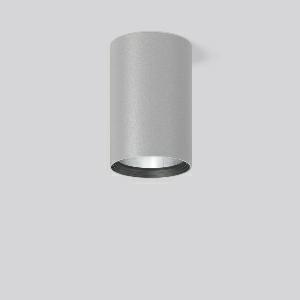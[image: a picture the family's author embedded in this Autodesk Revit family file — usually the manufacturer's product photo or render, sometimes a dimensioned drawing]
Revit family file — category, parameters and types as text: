
# Revit family: heledon_maxi_a_931224_004_76_19c8
name_source: partatom
category: Lighting Fixtures
units: mm (PartAtom-declared; Revit-internal decimal feet)

## family parameters
Cut with Voids When Loaded = No
Host = Face
Light Source = No
Part Type = Normal
Room Calculation Point = No
Round Connector Dimension = Use Diameter
Shared = No

## types (1)
- HELEDON maxi A (1 x LED Modul 930, 4300 lm, 3000)
    Apparent Load = 35 VA
    Approval mark = CE
    CIE Flux Codes = 100 100 100 100 100
    Color Rendering = 90
    Color Temperature = 3000
    Default Elevation = 1800 mm
    Description = Series: HELEDON maxi
Cylindrical surface-mounted downlight. Housing: die-cast aluminium, powder-coated. Internal ceiling frame polycarbonate with bayonet mounting. Black plastic ring and recessed LED to prevent glare from the side. Optical assembly with reflector made of MIRO-Silver with 98% total light reflection for outstanding efficiency - can be changed without tools. Best colour rendering index Ra>90. Suitable for Ceiling mounting. Easy installation with a separate ceiling frame with bayonet mounting and plug connection. Driver integrated. Connected via plug-in connector. High quality converter without flickering and stroboscopic effect. The following accessories can be mounted without use of tools: interchangeable lenses, decorative glasses, honeycomb louvre, clear and frosted diffusers, white interchangeable plastic ring. 
Colour: silver
Diameter: 123 mm
Height: 183 mm
Lamp: LED
Socket: without socket
Colour temperature: 3000K
Colour rendering index (CRI): 92
System power: 35 W
Rated luminous flux: 4300 lm
Luminous efficiency: 123 lm/W
Control gear: Converter, dimmable, DALI
Protection class: I
Type of protection: IP 20
    Height = 183 mm
    Lamp = 1 x LED Modul 930
    Lamp Light Flux = 4300 lm
    Lamp count = 1
    Length = 123 mm
    Lifetime = 50000 h
    Luminous efficacy = 123 lm/W
    Manufacturer = RZB
    ModVariant = No
    Model = 931224.004.76
    Mounting Place = Ceiling
    Mounting Type = Surface mounted
    Number of Poles = 1
    OnlyDefault = Yes
    Power Factor = 1
    Product Name = HELEDON maxi A
    Product group = Surface mounted downlights
    ProductGroupID = 302
    Protection Class = Protection class I
    Protection Degree = IP 20
    RLX_Detail_Level = 1
    RLX_Emergency_Light_Flux = 0 lm
    RLX_Emergency_Type = 0
    RLX_Emergency_Type_DB = No
    RlxData = <blob elided: 100297 chars, md5=e5b779f6>
    Socket = socket
    Standby Power = 0 W
    System Light Flux = 4300 lm
    System Power = 35 W
    Type Comments = Product without accessories
    Type Image = 931192.004.jpg
    URL = http://relux.com
    VarID = ---
    Voltage = 230 V
    Voltage Range = 220-240 V
    Weight = 0.00 kg
    Width = 0 mm  [stored 0 ft]

note: [stored X ft] marks values corroborated as IEEE doubles in the binary element streams (Revit-internal decimal feet)

## geometry (parser evidence)
native form markers: Blend x4, Sweep x11
no freeform markers — native parametric forms only
